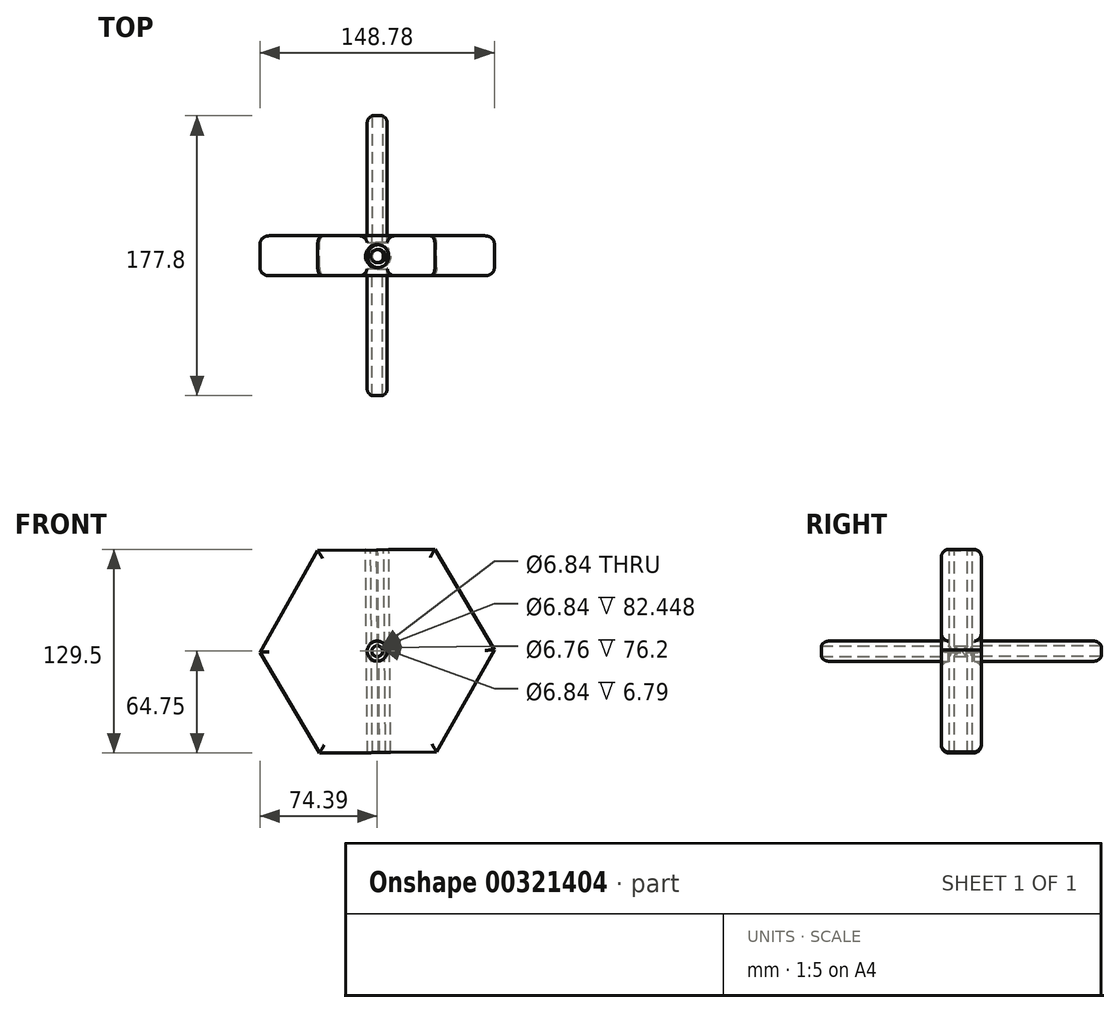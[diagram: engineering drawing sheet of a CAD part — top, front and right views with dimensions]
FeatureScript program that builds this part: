
annotation { "Feature Type Name" : "Feature", "Feature Type Description" : "" }
export const myFeature = defineFeature(function(context is Context, id is Id, definition is map)
    precondition{}
    {
        {
            var Q0;
            Q0=qCreatedBy(makeId("Front.planeOp"),FACE);
            var sketch = newSketch(context, id + "F0", { "sketchPlane" : qUnion([Q0])});
            skCircle(sketch, "E0.cCircle", {"center": v(0, 0) * mm, "radius": 64.43 * mm, "construction": true});
            skLineSegment(sketch, "E0.0", {"start": v(74.4, 0.66) * mm, "end": v(37.76, -64.1) * mm});
            skLineSegment(sketch, "E0.1", {"start": v(37.76, -64.1) * mm, "end": v(-36.63, -64.75) * mm});
            skLineSegment(sketch, "E0.2", {"start": v(-36.63, -64.75) * mm, "end": v(-74.4, -0.66) * mm});
            skLineSegment(sketch, "E0.3", {"start": v(-74.4, -0.66) * mm, "end": v(-37.76, 64.1) * mm});
            skLineSegment(sketch, "E0.4", {"start": v(-37.76, 64.1) * mm, "end": v(36.63, 64.75) * mm});
            skLineSegment(sketch, "E0.5", {"start": v(36.63, 64.75) * mm, "end": v(74.4, 0.66) * mm});
            skPoint(sketch, "E0.0.midPoint", {"position": v(56.08, -31.72) * mm});
            skCircle(sketch, "E1", {"center": v(0, 0) * mm, "radius": 6.35 * mm});
            skSolve(sketch);
        }
        {
            var Q0;
            Q0=makeQuery(id+"F0.imprint","IMPRINT",FACE,{"disambiguationData":[TD([[makeQuery(id+"F0.imprint","IMPRINT",EDGE,{"derivedFrom":sQuery(id+"F0.wireOp",EDGE,"E0.0")}),-1.0]])]});
            extrude(context, id + "F1", {"entities" : qUnion([Q0]), "depth" : 25.4 * mm});
        }
        {
            var Q0;
            Q0=makeQuery(id+"F1.opExtrude","CAP_FACE",FACE,{"disambiguationData":[OSD([sQuery(id+"F0.wireOp",EDGE,"E0.0"),sQuery(id+"F0.wireOp",EDGE,"E0.1"),sQuery(id+"F0.wireOp",EDGE,"E0.2"),sQuery(id+"F0.wireOp",EDGE,"E0.3"),sQuery(id+"F0.wireOp",EDGE,"E0.4"),sQuery(id+"F0.wireOp",EDGE,"E0.5"),sQuery(id+"F0.wireOp",EDGE,"E1")])],"isStart":false});
            fillet(context, id + "F2", {"entities" : qUnion([Q0]), "radius" : 5.08 * mm, "tangentPropagation" : true, "allowEdgeOverflow" : false});
        }
        {
            var Q0;
            Q0=makeQuery(id+"F1.opExtrude","CAP_FACE",FACE,{"disambiguationData":[OSD([sQuery(id+"F0.wireOp",EDGE,"E0.0"),sQuery(id+"F0.wireOp",EDGE,"E0.1"),sQuery(id+"F0.wireOp",EDGE,"E0.2"),sQuery(id+"F0.wireOp",EDGE,"E0.3"),sQuery(id+"F0.wireOp",EDGE,"E0.4"),sQuery(id+"F0.wireOp",EDGE,"E0.5"),sQuery(id+"F0.wireOp",EDGE,"E1")])],"isStart":true});
            fillet(context, id + "F3", {"entities" : qUnion([Q0]), "radius" : 5.08 * mm, "tangentPropagation" : true, "allowEdgeOverflow" : false});
        }
        {
            var Q0;
            Q0=qCreatedBy(makeId("Front.planeOp"),FACE);
            var sketch = newSketch(context, id + "F4", { "sketchPlane" : qUnion([Q0])});
            skCircle(sketch, "E2", {"center": v(0, 0) * mm, "radius": 6.4 * mm});
            skSolve(sketch);
        }
        {
            var Q0;
            Q0 = qSketchRegion(id + "F4", true);
            extrude(context, id + "F5", {"entities" : qUnion([Q0]), "operationType" : NewBodyOperationType.ADD, "depth" : 101.6 * mm});
        }
        {
            var Q0;
            Q0=qCreatedBy(makeId("Front.planeOp"),FACE);
            var sketch = newSketch(context, id + "F6", { "sketchPlane" : qUnion([Q0])});
            skCircle(sketch, "E3", {"center": v(0, 0) * mm, "radius": 6.39 * mm});
            skSolve(sketch);
        }
        {
            var Q0;
            Q0 = qSketchRegion(id + "F6", true);
            extrude(context, id + "F7", {"entities" : qUnion([Q0]), "operationType" : NewBodyOperationType.ADD, "oppositeDirection" : true, "depth" : 76.2 * mm});
        }
        {
            var Q0;
            Q0=qCreatedBy(makeId("Front.planeOp"),FACE);
            var sketch = newSketch(context, id + "F8", { "sketchPlane" : qUnion([Q0])});
            skCircle(sketch, "E4", {"center": v(0, 0) * mm, "radius": 3.38 * mm});
            skSolve(sketch);
        }
        {
            var Q0;
            Q0 = qSketchRegion(id + "F8", true);
            extrude(context, id + "F9", {"entities" : qUnion([Q0]), "operationType" : NewBodyOperationType.REMOVE, "endBound" : BoundingType.THROUGH_ALL, "oppositeDirection" : true, "depth" : 228.6 * mm});
        }
        {
            var Q0;
            Q0=qCreatedBy(makeId("Front.planeOp"),FACE);
            var sketch = newSketch(context, id + "F10", { "sketchPlane" : qUnion([Q0])});
            skCircle(sketch, "E5", {"center": v(0, 0) * mm, "radius": 3.42 * mm});
            skSolve(sketch);
        }
        {
            var Q0;
            Q0 = qSketchRegion(id + "F10", true);
            extrude(context, id + "F11", {"entities" : qUnion([Q0]), "operationType" : NewBodyOperationType.REMOVE, "depth" : 228.6 * mm});
        }
        {
            var Q0;
            Q0=makeQuery(id+"F7.opExtrude","CAP_EDGE",EDGE,{"disambiguationData":[OSD([sQuery(id+"F6.wireOp",EDGE,"E3")])],"isStart":false});
            var Q1;
            Q1=makeQuery(id+"F5.opExtrude","CAP_EDGE",EDGE,{"disambiguationData":[OSD([sQuery(id+"F4.wireOp",EDGE,"E2")])],"isStart":false});
            fillet(context, id + "F12", {"entities" : qUnion([Q0, Q1]), "radius" : 5.08 * mm, "tangentPropagation" : true, "allowEdgeOverflow" : false});
        }
        {
            var Q0;
            Q0=makeQuery(id+"F1.opExtrude","SWEPT_FACE",FACE,{"disambiguationData":[OSD([sQuery(id+"F0.wireOp",EDGE,"E0.4")])]});
            var sketch = newSketch(context, id + "F13", { "sketchPlane" : qUnion([Q0])});
            skCircle(sketch, "E6", {"center": v(0.57, -12.97) * mm, "radius": 7.36 * mm});
            skCircle(sketch, "E7", {"center": v(0.57, -12.97) * mm, "radius": 4.16 * mm});
            skSolve(sketch);
        }
        {
            var Q0;
            Q0=makeQuery(id+"F13.imprint","IMPRINT",FACE,{"disambiguationData":[TD([[makeQuery(id+"F13.imprint","IMPRINT",EDGE,{"derivedFrom":sQuery(id+"F13.wireOp",EDGE,"E7")}),-1.0]])]});
            extrude(context, id + "F14", {"entities" : qUnion([Q0]), "operationType" : NewBodyOperationType.REMOVE, "oppositeDirection" : true, "depth" : 228.6 * mm});
        }
    });
